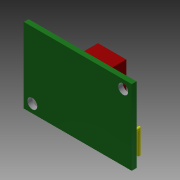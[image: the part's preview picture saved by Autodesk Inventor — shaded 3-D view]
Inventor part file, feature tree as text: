
AUTODESK INVENTOR PART (.ipt)
format: ipt  version: 2015 (Build 190159000, 159)  size: 167,424 bytes
history: native  units: mm
features: sketch x3, extrude x3, sweep x1
ambient origin geometry x8: Origin, YZ Plane, XZ Plane, XY Plane, X Axis, Y Axis, Z Axis, Center Point
bodies: Solid1 (feature_tree)
feature tree (7):
  sketch  "Sketch1"  dims[d0=38.0mm d1=26.416mm]
  extrude  "Extrusion1"  Depth=26.416mm
  extrude  "Extrusion2"  Depth=3.5mm
  extrude  "Extrusion3"  Depth=4.1mm
  sweep  "Sweep1"
  sketch  "Sketch3"  dims[d4=3.0mm d5=3.0mm d6=3.0mm d7=3.0mm d8=1.0mm d9=4.572mm d10=4.69mm d11=50.0mm d13=2.54mm d14=10.0mm d16=10.0mm d18=1.27mm d19=1.27mm d20=1.27mm d21=1.27mm d22=1.0mm d23=11.176mm d24=30.0mm d26=2.54mm d27=10.0mm d29=10.0mm d31=1.27mm d33=1.27mm d34=9.96mm d35=11.66mm d36=3.74mm d37=1.7mm d38=0.0mm d39=8.62mm d40=0.0mm d41=4.1mm d42=0.0mm d43=6.15mm d44=7.87mm d45=0.0mm d46=0.0mm]
  sketch  "Sketch2"  dims[d2=3.5mm d3=3.5mm]
